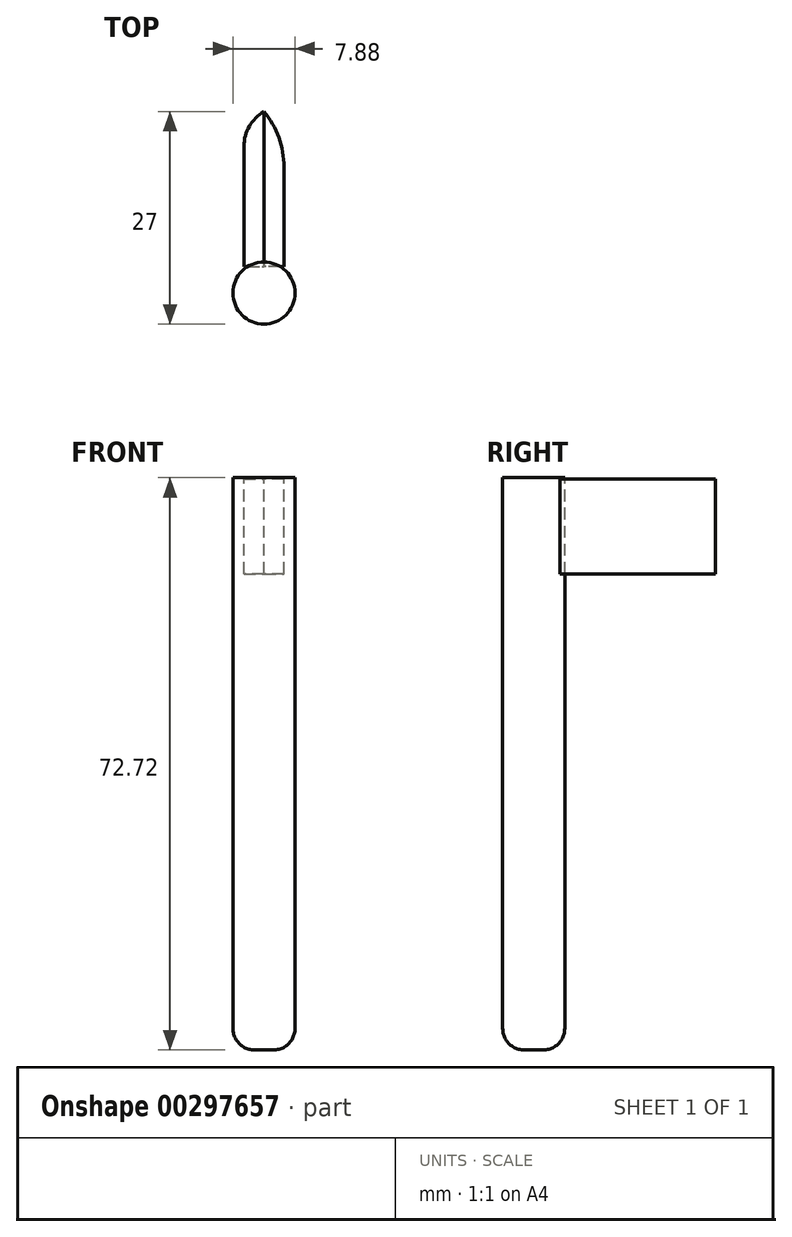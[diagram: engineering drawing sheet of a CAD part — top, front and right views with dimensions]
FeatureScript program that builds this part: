
annotation { "Feature Type Name" : "Feature", "Feature Type Description" : "" }
export const myFeature = defineFeature(function(context is Context, id is Id, definition is map)
    precondition{}
    {
        {
            var Q0;
            Q0=qCreatedBy(makeId("Right.planeOp"),FACE);
            var sketch = newSketch(context, id + "F0", { "sketchPlane" : qUnion([Q0])});
            skLineSegment(sketch, "E0", {"start": v(-34.3, 43.36) * mm, "end": v(-34.3, -29.36) * mm});
            skLineSegment(sketch, "E1", {"start": v(-34.3, -29.36) * mm, "end": v(-30.35, -29.36) * mm});
            skLineSegment(sketch, "E2", {"start": v(-30.35, -29.36) * mm, "end": v(-30.35, 43.36) * mm});
            skLineSegment(sketch, "E3", {"start": v(-30.35, 43.36) * mm, "end": v(-34.3, 43.36) * mm});
            skSolve(sketch);
        }
        {
            var Q0;
            Q0=makeQuery(id+"F0.imprint","IMPRINT",FACE,{"disambiguationData":[TD([[makeQuery(id+"F0.imprint","IMPRINT",EDGE,{"derivedFrom":sQuery(id+"F0.wireOp",EDGE,"E0")}),1.0]])]});
            var Q1;
            Q1=sQuery(id+"F0.wireOp",EDGE,"E2");
            revolve(context, id + "F1", {"entities" : qUnion([Q0]), "axis" : qUnion([Q1]), "revolveType" : RevolveType.FULL, "oppositeDirection" : true});
        }
        {
            var Q0;
            Q0=qCreatedBy(makeId("Right.planeOp"),FACE);
            var sketch = newSketch(context, id + "F2", { "sketchPlane" : qUnion([Q0])});
            skLineSegment(sketch, "E4", {"start": v(-27, 43.16) * mm, "end": v(-7.3, 43.16) * mm});
            skLineSegment(sketch, "E5", {"start": v(-7.3, 43.16) * mm, "end": v(-7.3, 31.14) * mm});
            skLineSegment(sketch, "E6", {"start": v(-7.3, 31.14) * mm, "end": v(-27, 31.14) * mm});
            skLineSegment(sketch, "E7", {"start": v(-27, 31.14) * mm, "end": v(-27, 43.16) * mm});
            skSolve(sketch);
        }
        {
            var Q0;
            Q0=makeQuery(id+"F2.imprint","IMPRINT",FACE,{"disambiguationData":[TD([[makeQuery(id+"F2.imprint","IMPRINT",EDGE,{"derivedFrom":sQuery(id+"F2.wireOp",EDGE,"E4")}),-1.0]])]});
            extrude(context, id + "F3", {"entities" : qUnion([Q0]), "depth" : 2.54 * mm});
        }
        {
            var Q0;
            Q0=makeQuery(id+"F3.opExtrude","CAP_EDGE",EDGE,{"disambiguationData":[OSD([sQuery(id+"F2.wireOp",EDGE,"E5")])],"isStart":false});
            fillet(context, id + "F4", {"entities" : qUnion([Q0]), "radius" : 11.04 * mm, "tangentPropagation" : true, "allowEdgeOverflow" : false});
        }
        {
            var Q0;
            Q0=makeQuery(id+"F2.imprint","IMPRINT",FACE,{"disambiguationData":[TD([[makeQuery(id+"F2.imprint","IMPRINT",EDGE,{"derivedFrom":sQuery(id+"F2.wireOp",EDGE,"E4")}),-1.0]])]});
            extrude(context, id + "F5", {"entities" : qUnion([Q0]), "oppositeDirection" : true, "depth" : 2.54 * mm});
        }
        {
            var Q0;
            Q0=makeQuery(id+"F5.opExtrude","CAP_EDGE",EDGE,{"disambiguationData":[OSD([sQuery(id+"F2.wireOp",EDGE,"E5")])],"isStart":false});
            fillet(context, id + "F6", {"entities" : qUnion([Q0]), "radius" : 5.08 * mm, "tangentPropagation" : true, "allowEdgeOverflow" : false});
        }
        {
            var Q0;
            Q0=makeQuery(id+"F1.opRevolve","SWEPT_FACE",FACE,{"disambiguationData":[OSD([sQuery(id+"F0.wireOp",EDGE,"E1")])]});
            fillet(context, id + "F7", {"entities" : qUnion([Q0]), "radius" : 2.76 * mm, "tangentPropagation" : true, "allowEdgeOverflow" : false});
        }
    });
